# Revit family: BLAUBERG-KOMFORT_EC_D5B_180
name_source: partatom
category: Mechanical Equipment
units: mm (PartAtom-declared; Revit-internal decimal feet)

## family parameters
Always vertical = No
Classification = None
Cut with Voids When Loaded = No
OmniClass Number = 23.75.35.14
OmniClass Title = Air Handling Units
Part Type = Normal
Room Calculation Point = No
Round Connector Dimension = Use Diameter
Shared = No
Work Plane-Based = No

## types (4) — shared parameters
A = 1009 mm  [stored 3.31037 ft]
A1 = 900 mm  [stored 2.95276 ft]
B = 600 mm  [stored 1.9685 ft]
B1 = 326 mm  [stored 1.06955 ft]
B2 = 163 mm  [stored 0.534777 ft]
Casing Material = Polypropylene Black
Current = 1 A
D = 150 mm
Ddrain = 20 mm  [stored 0.0656168 ft]
Description = Air Handling Unit
Duct Connection Diameter = 150 mm
DuctConL = 55 mm
Extract Air Filter = G4
Family Version = 1.0
Front Maintenance Zone Height = 600 mm  [stored 1.9685 ft]
Front Maintenance Zone Length = 900 mm  [stored 2.95276 ft]
Front Maintenance Zone Width = 600 mm  [stored 1.9685 ft]
H = 264 mm  [stored 0.866142 ft]
H1 = 250 mm  [stored 0.82021 ft]
H2 = 110 mm  [stored 0.360892 ft]
Heat Exchanger Type = counter-flow
Load Classification = HVAC
Maintenance Zone Material = Maintenance Zone
Manufacturer = Blauberg
Maximum Air Flow = 220 m³/h
Metal Material = Metal Zinc
Number of Poles = 1
Power = 87 W
Power Factor = 1
RPM (min-1) = 2200
SEC Class = A+
Side Maintenance Zone Height = 350 mm  [stored 1.14829 ft]
Side Maintenance Zone Length = 900 mm  [stored 2.95276 ft]
Side Maintenance Zone Width = 250 mm  [stored 0.82021 ft]
Sound Pressure Level at 3 m (dBA) = 33
Supply Air Filter = G4+F7
Transported Air Temperature (°C) = –25 …+40
URL = https://blaubergventilatoren.de
Voltage = 230 V
Weight = 14.00 kg

## per-type parameters (varying)
| type | Drain Connection Diameter | DrainPipe1 | DrainPipe2 | Heat Exchanger Material | Heat recovery efficiency (%) | Type Comments |
| KOMFORT EC D5B 180 S21 | 19 mm  [stored 0.062336 ft] | Yes | Yes | polystyrene | 86..98 | Air Handling Unit KOMFORT EC D5B 180 S21 |
| KOMFORT EC D5B 180 S14 | 19 mm  [stored 0.062336 ft] | Yes | Yes | polystyrene | 86..98 | Air Handling Unit KOMFORT EC D5B 180 S14 |
| KOMFORT EC D5B 180-E S21 | 0 mm  [stored 0 ft] | No | No | enthalpy | 79..94 | Air Handling Unit KOMFORT EC D5B 180-E S21 |
| KOMFORT EC D5B 180-E S14 | 0 mm  [stored 0 ft] | No | No | enthalpy | 79..94 | Air Handling Unit KOMFORT EC D5B 180-E S14 |

note: column(s) folded — value = type name in every type: Model

note: [stored X ft] marks values corroborated as IEEE doubles in the binary element streams (Revit-internal decimal feet)

## geometry (parser evidence)
native form markers: Sweep x6
no freeform markers — native parametric forms only
